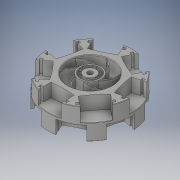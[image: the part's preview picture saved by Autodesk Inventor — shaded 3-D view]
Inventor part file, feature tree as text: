
AUTODESK INVENTOR PART (.ipt)
format: ipt  version: 2018 (Build 220112000, 112)  size: 905,728 bytes
history: native  units: in
note: dims shown in document units (in); Inventor stores cm internally (conversion verified against a paired STEP export)
features: sketch x12, extrude x11, pattern_circular x2, mirror x1, revolve x1, chamfer x1, fillet x1, projected_geometry x1
ambient origin geometry x8: Origin, YZ Plane, XZ Plane, XY Plane, X Axis, Y Axis, Z Axis, Center Point
bodies: Solid1 (feature_tree)
feature tree (30):
  extrude  "Extrusion1"  Depth=1.3386in
  extrude  "Extrusion2"  Depth=0.374in
  extrude  "Extrusion3"  Depth=0.9055in TaperAngle=0.0deg
  extrude  "Extrusion4"  Depth=2.3622in TaperAngle=360.0deg
  mirror  "Mirror1"
  extrude  "Extrusion5"  Depth=2.3622in TaperAngle=360.0deg
  revolve  "Revolution1"  [1 undecoded]
  extrude  "Extrusion6"  Depth=0.9055in TaperAngle=0.0deg
  extrude  "Extrusion7"  Depth=0.0177in
  extrude  "Extrusion8"  Depth=0.0197in
  chamfer  "Chamfer1"  Distance=0.3937in
  extrude  "Extrusion9"  Depth=0.0354in TaperAngle=0.0deg
  pattern_circular  "Circular Pattern1"  [2 undecoded]
  extrude  "Extrusion10"  Depth=0.0787in TaperAngle=45.0deg
  pattern_circular  "Circular Pattern2"  [2 undecoded]
  fillet  "Fillet2"  Radius=0.4331in
  extrude  "Extrusion11"  Depth=0.0118in
  sketch  "Sketch1"  dims[d0=1.4567in d1=1.3386in]
  sketch  "Sketch2"  dims[d2=0.9055in d3=0.0in d4=0.374in]
  sketch  "Sketch3"  dims[d5=0.1575in d6=0.9055in d7=0.0in]
  sketch  "Sketch4"  dims[d8=0.6693in d9=2.3622in d11=360.0deg]
  sketch  "Sketch5"  dims[d13=0.8661in d14=0.0in d15=2.3622in d17=360.0deg]
  sketch  "Sketch6"  dims[d19=0.2756in d20=0.0in d21=0.5906in]
  sketch  "Sketch7"  dims[d22=0.6693in d23=0.9055in d24=0.0in]
  sketch  "Sketch8"  dims[d25=0.0591in d26=0.0177in]
  sketch  "Sketch9"  dims[d27=0.0177in d28=0.0197in]
  sketch  "Sketch10"  dims[d29=90.0deg d30=0.3937in d31=0.0in]
  sketch  "Sketch11"  dims[d32=2.3622in d34=360.0deg d36=0.0354in d37=0.0in]
  projected_geometry  "Projected Loop1"
  sketch  "Sketch12"  dims[d38=2.5591in d39=0.9055in d40=0.0in d42=0.0157in d43=0.0787in d44=45.0deg d45=1.1024in d48=0.4331in d49=0.4331in d50=0.0394in d51=0.0394in d52=0.0787in d53=0.0787in d54=0.0394in d58=0.2854in d59=0.2854in d60=0.2657in d61=0.2657in d62=1.3878in d64=0.2756in d65=1.378in d66=0.4134in d67=0.0in d68=2.7559in d69=360.0deg d71=0.1767in d72=0.4134in d73=0.0in d74=2.7559in d75=360.0deg d77=0.0118in d78=2.4562in d79=0.0in]
note: 5 required parameter values undecoded (feature->parameter linkage not recoverable at this tier; creation-order binding heuristic only, values carry confidence <= 0.55)